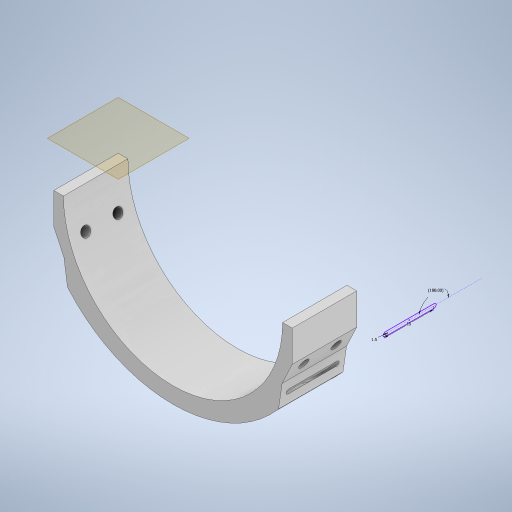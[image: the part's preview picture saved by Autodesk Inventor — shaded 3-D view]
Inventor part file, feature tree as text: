
AUTODESK INVENTOR PART (.ipt)
format: ipt  version: 2023 (Build 270158030, 158C)  size: 395,264 bytes
history: native  units: in
note: dims shown in document units (in); Inventor stores cm internally (conversion verified against a paired STEP export)
features: sketch x8, extrude x4, plane x1, sweep x1
ambient origin geometry x8: Origin, YZ Plane, XZ Plane, XY Plane, X Axis, Y Axis, Z Axis, Center Point
bodies: Solid1 (feature_tree)
feature tree (14):
  extrude  "Extrusion1"  Depth=3.5433in
  extrude  "Extrusion2"  Depth=0.1181in
  extrude  "Extrusion3"  Depth=0.7874in TaperAngle=0.0deg
  plane  "Work Plane1"
  extrude  "Extrusion5"  Depth=0.1969in
  sketch  "Sketch6"  dims[d38=0.1181in d39=0.3937in]
  sketch  "Sketch7"  dims[d40=0.1181in]
  sweep  "Sweep2"
  sketch  "Sketch1"  dims[d0=2.6772in d1=1.3386in d2=0.3078in d3=0.3078in d4=0.1832in d5=0.1832in d6=0.1484in d7=0.1484in d8=0.7916in d9=0.7916in d10=0.2913in d11=90.0deg d12=90.0deg d13=0.126in d14=90.0deg d15=0.126in d16=90.0deg d17=0.2707in d18=90.0deg d19=0.2707in d20=90.0deg d21=0.0787in d22=0.1969in d23=0.1969in d24=1.2297in d28=0.1575in d29=3.5433in]
  sketch  "Sketch2"  dims[d30=0.1181in d32=0.1181in]
  sketch  "Sketch3"  dims[d33=0.3836in d34=0.7874in d35=0.0in]
  sketch  "Sketch5"  dims[d36=0.1181in d37=0.1969in]
  sketch  "Sketch9"  dims[d41=0.3937in]
  sketch  "Sketch10"  dims[d42=0.1181in d43=0.3937in d44=0.1181in d45=0.3937in d46=0.0in d47=0.0in d48=0.1181in d49=0.1969in d50=0.1181in d51=0.3937in d52=0.1181in d53=0.3937in d54=0.1181in d55=0.3937in d56=0.1181in d57=0.3937in d58=0.3937in d59=0.0in d71=0.1575in d72=0.0in d73=0.5906in d74=180.0deg d75=0.0591in d77=0.5906in d78=0.0in d79=0.0591in d80=0.0984in d81=1.6535in d82=0.0in d85=0.1181in d86=0.1181in d87=0.0984in d88=0.0984in d89=0.5906in d90=0.0591in d91=0.0984in d92=0.0in d93=0.0in]
